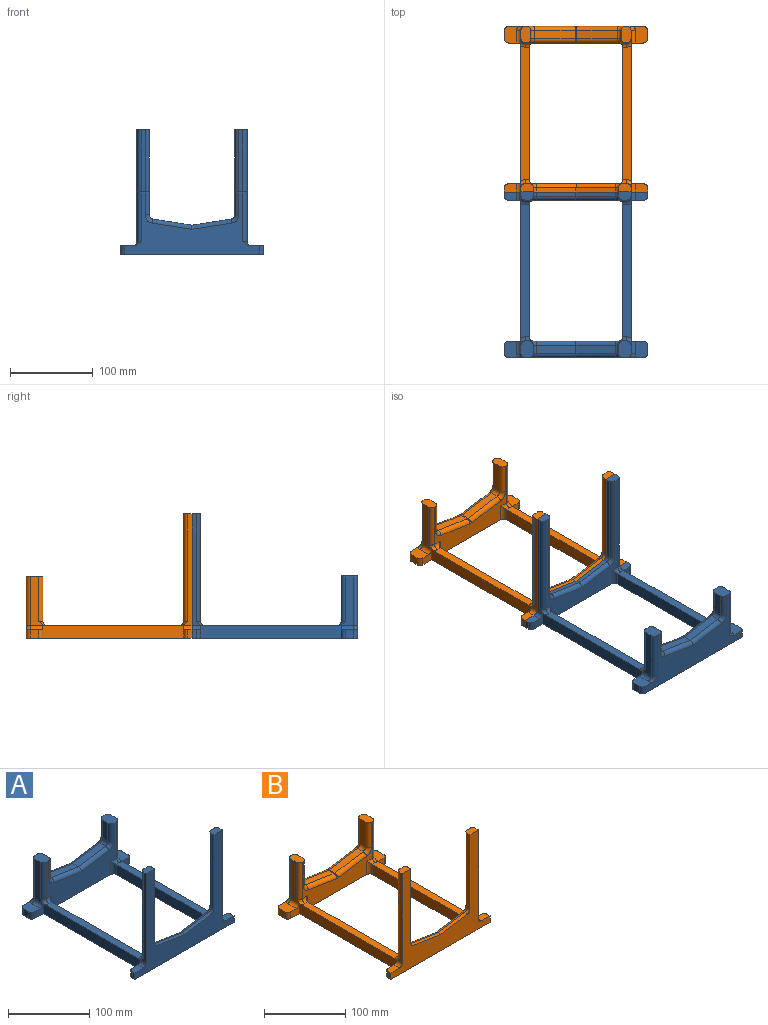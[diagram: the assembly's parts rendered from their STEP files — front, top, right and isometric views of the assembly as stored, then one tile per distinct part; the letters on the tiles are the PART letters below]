
ASSEMBLY  parts=2 mates=1
PART A: 87 faces, bbox 173x209.7x150 mm
  f0: plane 163x75mm, normal (0,1,0), area 5088.7mm2, adj f4,f26,f27,f29,f33,f35,f36,f37
  f1: plane 195x150mm, normal (-1,0,0), area 3854.9mm2, adj f4,f13,f14,f15,f20,f26,f31,f53
  f2: plane 15x10mm, normal (0,0,1), area 144.6mm2, adj f3,f14,f20,f58,f85
  f3: plane 10x5mm, normal (-1,0,0), area 50mm2, adj f2,f4,f14,f58
  f4: plane 200x173mm, normal (0,0,-1), area 8579.3mm2, adj f0,f1,f3,f5,f7,f14,f16,f17
  f5: plane 10x5mm, normal (1,0,0), area 50mm2, adj f4,f6,f14,f57
  f6: plane 15x10mm, normal (0,0,1), area 144.6mm2, adj f5,f14,f21,f57,f86
  f7: plane 195x150mm, normal (1,0,0), area 3854.9mm2, adj f4,f8,f14,f18,f21,f27,f34,f56
  f8: plane 15x10mm, normal (0,0,1), area 139.3mm2, adj f7,f9,f14,f19,f62,f80
  f9: plane 112.72x5mm, normal (-1,0,0), area 563.6mm2, adj f8,f14,f64,f80
  f10: plane 47.27x7.34mm, normal (-0.15,0,0.99), area 239.2mm2, adj f11,f14,f64,f78
  f11: plane 47.27x7.34mm, normal (0.15,0,0.99), area 239.2mm2, adj f10,f14,f63,f77
  f12: plane 112.72x5mm, normal (1,0,0), area 563.6mm2, adj f13,f14,f63,f75
  f13: plane 15x10mm, normal (0,0,1), area 139.3mm2, adj f1,f12,f14,f19,f61,f75
  f14: plane 173x150mm, normal (0,-1,0), area 7905.1mm2, adj f1,f2,f3,f4,f5,f6,f7,f8
  f15: plane 162.68x10mm, normal (0,0,1), area 1604.3mm2, adj f1,f16,f67,f68,f73,f74
  f16: plane 160x15mm, normal (1,0,0), area 2400mm2, adj f4,f15,f54,f59
  f17: plane 160x15mm, normal (-1,0,0), area 2400mm2, adj f4,f18,f55,f60
  f18: plane 162.68x10mm, normal (0,0,1), area 1604.3mm2, adj f7,f17,f69,f70,f71,f72
  f19: plane 150x123mm, normal (0,1,0), area 3878.8mm2, adj f4,f8,f13,f59,f60,f61,f62,f67
  f20: plane 15x15mm, normal (0,1,0), area 155.4mm2, adj f1,f2,f4,f58,f85
  f21: plane 15x15mm, normal (0,1,0), area 155.4mm2, adj f4,f6,f7,f57,f86
  f22: plane 27.72x10mm, normal (-1,0,0), area 277.2mm2, adj f27,f39,f44,f45
  f23: plane 47.27x10mm, normal (-0.15,0,0.99), area 478.3mm2, adj f24,f38,f44,f48
  f24: plane 47.27x10mm, normal (0.15,0,0.99), area 478.3mm2, adj f23,f36,f41,f46
  f25: plane 27.72x10mm, normal (1,0,0), area 277.2mm2, adj f26,f35,f40,f41
  f26: plane 20x15mm, normal (0,0,1), area 278.5mm2, adj f0,f1,f25,f28,f35,f40,f53,f66
  f27: plane 20x15mm, normal (0,0,1), area 278.5mm2, adj f0,f7,f22,f28,f39,f45,f56,f65
  f28: plane 123x75mm, normal (0,-1,0), area 4258.8mm2, adj f4,f26,f27,f40,f43,f45,f46,f47
  f29: plane 20x16.34mm, normal (0,0,1), area 291.4mm2, adj f0,f30,f31,f49,f50,f81,f82
  f30: plane 10x10mm, normal (-1,0,0), area 100mm2, adj f4,f29,f49,f50
  f31: plane 15x15mm, normal (0,-1,0), area 155.4mm2, adj f1,f4,f29,f50,f81
  f32: plane 10x10mm, normal (1,0,0), area 100mm2, adj f4,f33,f51,f52
  f33: plane 20x16.34mm, normal (0,0,1), area 291.4mm2, adj f0,f32,f34,f51,f52,f83,f84
  f34: plane 15x15mm, normal (0,-1,0), area 155.4mm2, adj f4,f7,f33,f52,f83
  f35: cylinder r=5mm len=27.72mm, axis (0,0,1), area 217.7mm2, adj f0,f25,f26,f37
  f36: cylinder r=5mm len=48.8mm, axis (-0.99,0,0.15), area 378.7mm2, adj f0,f24,f37,f38
  f37: torus R=10mm, axis (0,-1,0), area 75.8mm2, adj f0,f35,f36,f41
  f38: cylinder r=5mm len=48.8mm, axis (-0.99,0,-0.15), area 378.7mm2, adj f0,f23,f36,f42
  f39: cylinder r=5mm len=27.72mm, axis (0,0,-1), area 217.7mm2, adj f0,f22,f27,f42
  f40: cylinder r=5mm len=27.72mm, axis (0,0,-1), area 217.7mm2, adj f25,f26,f28,f43
  f41: cylinder r=5mm len=10mm, axis (0,-1,0), area 70.8mm2, adj f24,f25,f37,f43
  f42: torus R=10mm, axis (0,-1,0), area 75.8mm2, adj f0,f38,f39,f44
  f43: torus R=10mm, axis (0,-1,0), area 75.8mm2, adj f28,f40,f41,f46
  f44: cylinder r=5mm len=10mm, axis (0,1,0), area 70.8mm2, adj f22,f23,f42,f47
  f45: cylinder r=5mm len=27.72mm, axis (0,0,1), area 217.7mm2, adj f22,f27,f28,f47
  f46: cylinder r=5mm len=48.8mm, axis (0.99,0,-0.15), area 378.7mm2, adj f24,f28,f43,f48
  f47: torus R=10mm, axis (0,-1,0), area 75.8mm2, adj f28,f44,f45,f48
  f48: cylinder r=5mm len=48.8mm, axis (0.99,0,0.15), area 378.7mm2, adj f23,f28,f46,f47
  f49: cylinder r=5mm len=10mm, axis (0,0,-1), area 78.5mm2, adj f0,f4,f29,f30
  f50: cylinder r=5mm len=10mm, axis (0,0,1), area 78.5mm2, adj f4,f29,f30,f31
  f51: cylinder r=5mm len=10mm, axis (0,0,1), area 78.5mm2, adj f0,f4,f32,f33
  f52: cylinder r=5mm len=10mm, axis (0,0,-1), area 78.5mm2, adj f4,f32,f33,f34
  f53: cylinder r=5mm len=55mm, axis (0,0,-1), area 432mm2, adj f1,f26,f28,f74
  f54: cylinder r=5mm len=20mm, axis (0,0,1), area 132.1mm2, adj f4,f16,f28,f73
  f55: cylinder r=5mm len=20mm, axis (0,0,-1), area 132.1mm2, adj f4,f17,f28,f71
  f56: cylinder r=5mm len=55mm, axis (0,0,-1), area 432mm2, adj f7,f27,f28,f72
  f57: cylinder r=5mm len=10mm, axis (0,0,1), area 78.5mm2, adj f4,f5,f6,f21
  f58: cylinder r=5mm len=10mm, axis (0,0,-1), area 78.5mm2, adj f2,f3,f4,f20
  f59: cylinder r=5mm len=20mm, axis (0,0,-1), area 132.1mm2, adj f4,f16,f19,f67
  f60: cylinder r=5mm len=20mm, axis (0,0,1), area 132.1mm2, adj f4,f17,f19,f69
  f61: cylinder r=5mm len=130mm, axis (0,0,1), area 1021mm2, adj f1,f13,f19,f68
  f62: cylinder r=5mm len=130mm, axis (0,0,1), area 1021mm2, adj f7,f8,f19,f70
  f63: cylinder r=5mm len=5mm, axis (0,-1,0), area 35.4mm2, adj f11,f12,f14,f76
  f64: cylinder r=5mm len=5mm, axis (0,-1,0), area 35.4mm2, adj f9,f10,f14,f79
  f65: cylinder r=5mm len=60mm, axis (0,0,1), area 471.2mm2, adj f0,f7,f27,f84
  f66: cylinder r=5mm len=60mm, axis (0,0,-1), area 471.2mm2, adj f0,f1,f26,f82
  f67: cylinder r=5mm len=10mm, axis (1,0,0), area 53.5mm2, adj f15,f19,f59,f68
  f68: torus R=10mm, axis (0,0,1), area 47mm2, adj f1,f15,f61,f67
  f69: cylinder r=5mm len=10mm, axis (1,0,0), area 53.5mm2, adj f18,f19,f60,f70
  f70: torus R=10mm, axis (0,0,-1), area 47mm2, adj f7,f18,f62,f69
  f71: cylinder r=5mm len=10mm, axis (-1,0,0), area 53.5mm2, adj f18,f28,f55,f72
  f72: torus R=10mm, axis (0,0,-1), area 47mm2, adj f7,f18,f56,f71
  f73: cylinder r=5mm len=10mm, axis (-1,0,0), area 53.5mm2, adj f15,f28,f54,f74
  f74: torus R=10mm, axis (0,0,1), area 47mm2, adj f1,f15,f53,f73
  f75: cylinder r=5mm len=112.72mm, axis (0,0,-1), area 885.3mm2, adj f12,f13,f19,f76
  f76: torus R=10mm, axis (0,-1,0), area 75.8mm2, adj f19,f63,f75,f77
  f77: cylinder r=5mm len=48.8mm, axis (-0.99,0,0.15), area 378.7mm2, adj f11,f19,f76,f78
  f78: cylinder r=5mm len=48.8mm, axis (-0.99,0,-0.15), area 378.7mm2, adj f10,f19,f77,f79
  f79: torus R=10mm, axis (0,-1,0), area 75.8mm2, adj f19,f64,f78,f80
  f80: cylinder r=5mm len=112.72mm, axis (0,0,-1), area 885.3mm2, adj f8,f9,f19,f79
  f81: cylinder r=5mm len=15mm, axis (0,1,0), area 117.8mm2, adj f1,f29,f31,f82
  f82: torus R=10mm, axis (0,0,-1), area 47mm2, adj f0,f29,f66,f81
  f83: cylinder r=5mm len=15mm, axis (0,1,0), area 117.8mm2, adj f7,f33,f34,f84
  f84: torus R=10mm, axis (0,0,1), area 47mm2, adj f0,f33,f65,f83
  f85: cylinder r=5mm len=10mm, axis (0,1,0), area 78.5mm2, adj f1,f2,f14,f20
  f86: cylinder r=5mm len=10mm, axis (0,1,0), area 78.5mm2, adj f6,f7,f14,f21
PART B: 90 faces, bbox 173x209.7x150 mm
  f0: plane 163x75mm, normal (0,1,0), area 3682.5mm2, adj f4,f24,f25,f29,f33,f35,f37,f54
  f1: plane 195x150mm, normal (-1,0,0), area 3854.9mm2, adj f4,f13,f14,f15,f20,f24,f31,f42
  f2: plane 15x10mm, normal (0,0,1), area 144.6mm2, adj f3,f14,f20,f47,f88
  f3: plane 10x5mm, normal (-1,0,0), area 50mm2, adj f2,f4,f14,f47
  f4: plane 200x173mm, normal (0,0,-1), area 8579.3mm2, adj f0,f1,f3,f5,f7,f14,f16,f17
  f5: plane 10x5mm, normal (1,0,0), area 50mm2, adj f4,f6,f14,f46
  f6: plane 15x10mm, normal (0,0,1), area 144.6mm2, adj f5,f14,f21,f46,f89
  f7: plane 195x150mm, normal (1,0,0), area 3854.9mm2, adj f4,f8,f14,f18,f21,f25,f34,f45
  f8: plane 15x10mm, normal (0,0,1), area 139.3mm2, adj f7,f9,f14,f19,f51,f83
  f9: plane 112.72x5mm, normal (-1,0,0), area 563.6mm2, adj f8,f14,f52,f83
  f10: plane 47.27x7.34mm, normal (-0.15,0,0.99), area 239.2mm2, adj f11,f14,f52,f81
  f11: plane 47.27x7.34mm, normal (0.15,0,0.99), area 239.2mm2, adj f10,f14,f53,f80
  f12: plane 112.72x5mm, normal (1,0,0), area 563.6mm2, adj f13,f14,f53,f78
  f13: plane 15x10mm, normal (0,0,1), area 139.3mm2, adj f1,f12,f14,f19,f50,f78
  f14: plane 173x150mm, normal (0,-1,0), area 7905.1mm2, adj f1,f2,f3,f4,f5,f6,f7,f8
  f15: plane 162.68x10mm, normal (0,0,1), area 1604.3mm2, adj f1,f16,f56,f57,f62,f63
  f16: plane 160x15mm, normal (1,0,0), area 2400mm2, adj f4,f15,f43,f48
  f17: plane 160x15mm, normal (-1,0,0), area 2400mm2, adj f4,f18,f44,f49
  f18: plane 162.68x10mm, normal (0,0,1), area 1604.3mm2, adj f7,f17,f58,f59,f60,f61
  f19: plane 150x123mm, normal (0,1,0), area 3878.8mm2, adj f4,f8,f13,f48,f49,f50,f51,f56
  f20: plane 15x15mm, normal (0,1,0), area 155.4mm2, adj f1,f2,f4,f47,f88
  f21: plane 15x15mm, normal (0,1,0), area 155.4mm2, adj f4,f6,f7,f46,f89
  f22: plane 49.5x10mm, normal (0.15,0,0.99), area 500.9mm2, adj f39,f40,f66,f73
  f23: plane 37.25x10mm, normal (1,0,0), area 372.5mm2, adj f24,f39,f64,f71
  f24: plane 20x12mm, normal (0,0,1), area 218.5mm2, adj f0,f1,f23,f28,f42,f55,f64,f71
  f25: plane 20x12mm, normal (0,0,1), area 218.5mm2, adj f0,f7,f26,f28,f45,f54,f70,f77
  f26: plane 37.25x10mm, normal (-1,0,0), area 372.5mm2, adj f25,f41,f70,f77
  f27: plane 49.5x10mm, normal (-0.15,0,0.99), area 500.9mm2, adj f40,f41,f68,f75
  f28: plane 123x75mm, normal (0,-1,0), area 2852.6mm2, adj f4,f24,f25,f42,f43,f44,f45,f60
  f29: plane 20x16.34mm, normal (0,0,1), area 291.4mm2, adj f0,f30,f31,f35,f36,f84,f85
  f30: plane 10x10mm, normal (-1,0,0), area 100mm2, adj f4,f29,f35,f36
  f31: plane 15x15mm, normal (0,-1,0), area 155.4mm2, adj f1,f4,f29,f36,f84
  f32: plane 10x10mm, normal (1,0,0), area 100mm2, adj f4,f33,f37,f38
  f33: plane 20x16.34mm, normal (0,0,1), area 291.4mm2, adj f0,f32,f34,f37,f38,f86,f87
  f34: plane 15x15mm, normal (0,-1,0), area 155.4mm2, adj f4,f7,f33,f38,f86
  f35: cylinder r=5mm len=10mm, axis (0,0,-1), area 78.5mm2, adj f0,f4,f29,f30
  f36: cylinder r=5mm len=10mm, axis (0,0,1), area 78.5mm2, adj f4,f29,f30,f31
  f37: cylinder r=5mm len=10mm, axis (0,0,1), area 78.5mm2, adj f0,f4,f32,f33
  f38: cylinder r=5mm len=10mm, axis (0,0,-1), area 78.5mm2, adj f4,f32,f33,f34
  f39: cylinder r=5mm len=10mm, axis (0,1,0), area 70.8mm2, adj f22,f23,f65,f72
  f40: cylinder r=5mm len=10mm, axis (0,1,0), area 15.4mm2, adj f22,f27,f67,f74
  f41: cylinder r=5mm len=10mm, axis (0,1,0), area 70.8mm2, adj f26,f27,f69,f76
  f42: cylinder r=5mm len=55mm, axis (0,0,-1), area 432mm2, adj f1,f24,f28,f63
  f43: cylinder r=5mm len=20mm, axis (0,0,1), area 132.1mm2, adj f4,f16,f28,f62
  f44: cylinder r=5mm len=20mm, axis (0,0,-1), area 132.1mm2, adj f4,f17,f28,f60
  f45: cylinder r=5mm len=55mm, axis (0,0,-1), area 432mm2, adj f7,f25,f28,f61
  f46: cylinder r=5mm len=10mm, axis (0,0,1), area 78.5mm2, adj f4,f5,f6,f21
  f47: cylinder r=5mm len=10mm, axis (0,0,-1), area 78.5mm2, adj f2,f3,f4,f20
  f48: cylinder r=5mm len=20mm, axis (0,0,-1), area 132.1mm2, adj f4,f16,f19,f56
  f49: cylinder r=5mm len=20mm, axis (0,0,1), area 132.1mm2, adj f4,f17,f19,f58
  f50: cylinder r=5mm len=130mm, axis (0,0,1), area 1021mm2, adj f1,f13,f19,f57
  f51: cylinder r=5mm len=130mm, axis (0,0,1), area 1021mm2, adj f7,f8,f19,f59
  f52: cylinder r=5mm len=5mm, axis (0,-1,0), area 35.4mm2, adj f9,f10,f14,f82
  f53: cylinder r=5mm len=5mm, axis (0,-1,0), area 35.4mm2, adj f11,f12,f14,f79
  f54: cylinder r=5mm len=60mm, axis (0,0,1), area 471.2mm2, adj f0,f7,f25,f87
  f55: cylinder r=5mm len=60mm, axis (0,0,-1), area 471.2mm2, adj f0,f1,f24,f85
  f56: cylinder r=5mm len=10mm, axis (1,0,0), area 53.5mm2, adj f15,f19,f48,f57
  f57: torus R=10mm, axis (0,0,1), area 47mm2, adj f1,f15,f50,f56
  f58: cylinder r=5mm len=10mm, axis (1,0,0), area 53.5mm2, adj f18,f19,f49,f59
  f59: torus R=10mm, axis (0,0,-1), area 47mm2, adj f7,f18,f51,f58
  f60: cylinder r=5mm len=10mm, axis (-1,0,0), area 53.5mm2, adj f18,f28,f44,f61
  f61: torus R=10mm, axis (0,0,-1), area 47mm2, adj f7,f18,f45,f60
  f62: cylinder r=5mm len=10mm, axis (-1,0,0), area 53.5mm2, adj f15,f28,f43,f63
  f63: torus R=10mm, axis (0,0,1), area 47mm2, adj f1,f15,f42,f62
  f64: cylinder r=5mm len=37.25mm, axis (0,0,-1), area 292.6mm2, adj f23,f24,f28,f65
  f65: torus R=10mm, axis (0,-1,0), area 75.8mm2, adj f28,f39,f64,f66
  f66: cylinder r=5mm len=50.27mm, axis (0.99,0,-0.15), area 393.4mm2, adj f22,f28,f65,f67
  f67: torus R=10mm, axis (0,-1,0), area 16.5mm2, adj f28,f40,f66,f68
  f68: cylinder r=5mm len=50.27mm, axis (0.99,0,0.15), area 393.4mm2, adj f27,f28,f67,f69
  f69: torus R=10mm, axis (0,-1,0), area 75.8mm2, adj f28,f41,f68,f70
  f70: cylinder r=5mm len=37.25mm, axis (0,0,1), area 292.6mm2, adj f25,f26,f28,f69
  f71: cylinder r=5mm len=37.25mm, axis (0,0,1), area 292.6mm2, adj f0,f23,f24,f72
  f72: torus R=10mm, axis (0,-1,0), area 75.8mm2, adj f0,f39,f71,f73
  f73: cylinder r=5mm len=50.27mm, axis (-0.99,0,0.15), area 393.4mm2, adj f0,f22,f72,f74
  f74: torus R=10mm, axis (0,-1,0), area 16.5mm2, adj f0,f40,f73,f75
  f75: cylinder r=5mm len=50.27mm, axis (-0.99,0,-0.15), area 393.4mm2, adj f0,f27,f74,f76
  f76: torus R=10mm, axis (0,-1,0), area 75.8mm2, adj f0,f41,f75,f77
  f77: cylinder r=5mm len=37.25mm, axis (0,0,-1), area 292.6mm2, adj f0,f25,f26,f76
  f78: cylinder r=5mm len=112.72mm, axis (0,0,1), area 885.3mm2, adj f12,f13,f19,f79
  f79: torus R=10mm, axis (0,-1,0), area 75.8mm2, adj f19,f53,f78,f80
  f80: cylinder r=5mm len=48.8mm, axis (-0.99,0,0.15), area 378.7mm2, adj f11,f19,f79,f81
  f81: cylinder r=5mm len=48.8mm, axis (-0.99,0,-0.15), area 378.7mm2, adj f10,f19,f80,f82
  f82: torus R=10mm, axis (0,-1,0), area 75.8mm2, adj f19,f52,f81,f83
  f83: cylinder r=5mm len=112.72mm, axis (0,0,-1), area 885.3mm2, adj f8,f9,f19,f82
  f84: cylinder r=5mm len=15mm, axis (0,1,0), area 117.8mm2, adj f1,f29,f31,f85
  f85: torus R=10mm, axis (0,0,-1), area 47mm2, adj f0,f29,f55,f84
  f86: cylinder r=5mm len=15mm, axis (0,1,0), area 117.8mm2, adj f7,f33,f34,f87
  f87: torus R=10mm, axis (0,0,1), area 47mm2, adj f0,f33,f54,f86
  f88: cylinder r=5mm len=10mm, axis (0,1,0), area 78.5mm2, adj f1,f2,f14,f20
  f89: cylinder r=5mm len=10mm, axis (0,1,0), area 78.5mm2, adj f6,f7,f14,f21
PLACE A rot(axis=(0,0,1),180deg) t=(156.6,-577.4,46.9)mm
PLACE B t=(156.6,-177.4,46.9)mm
MATE fastened A.f14 <-> B.f14  axis (0,1,0) through (97.6,-377.4,146.9)mm
